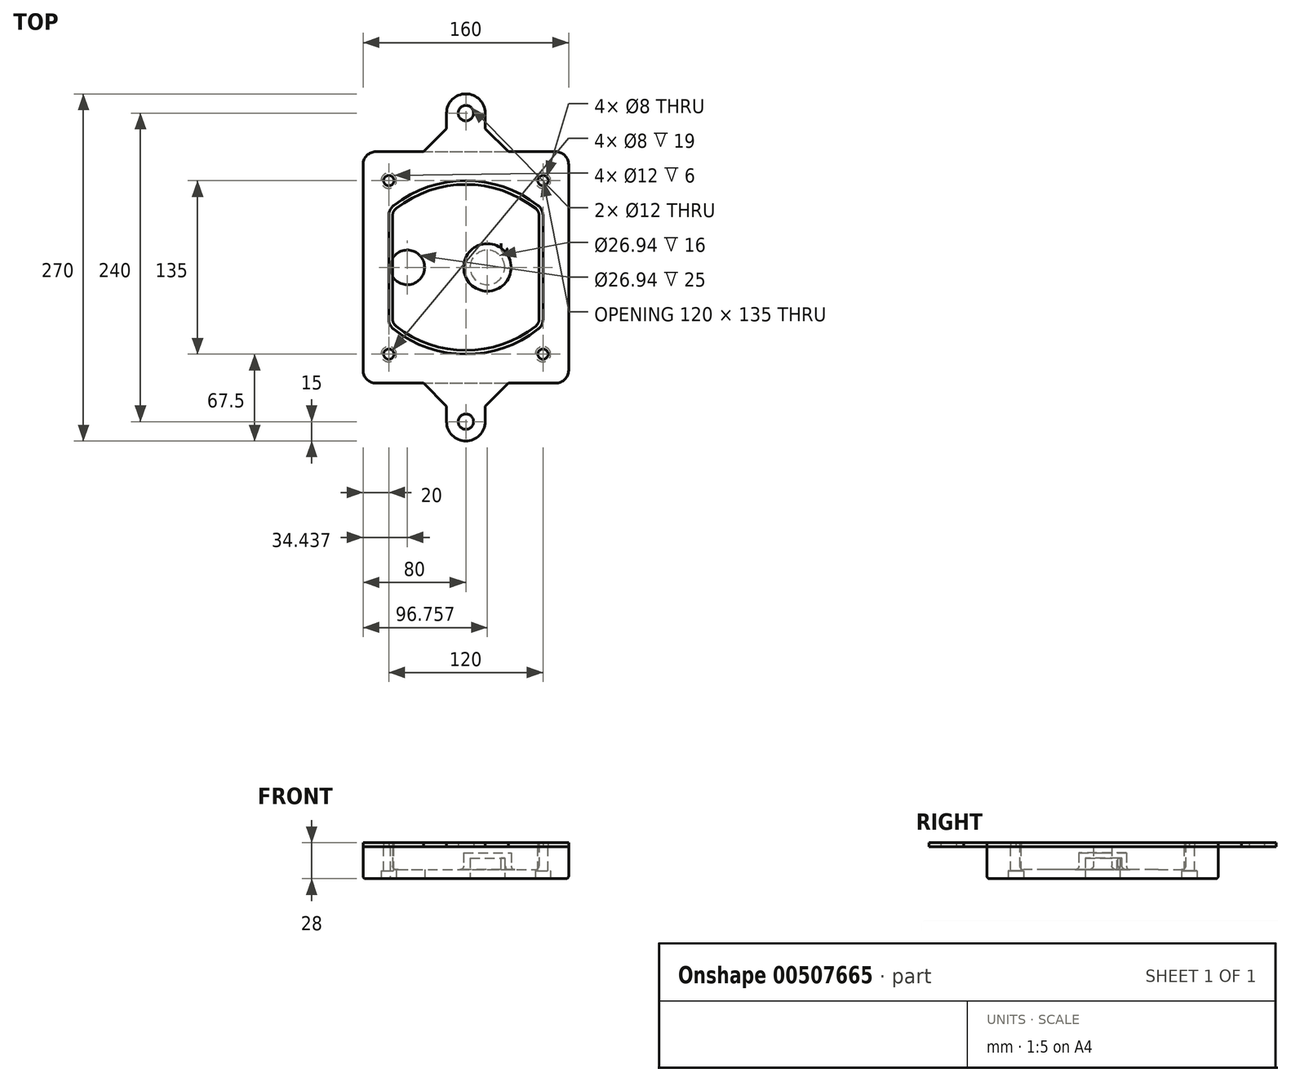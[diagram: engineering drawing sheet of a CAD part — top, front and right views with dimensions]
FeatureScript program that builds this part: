
annotation { "Feature Type Name" : "Feature", "Feature Type Description" : "" }
export const myFeature = defineFeature(function(context is Context, id is Id, definition is map)
    precondition{}
    {
        {
            var Q0;
            Q0=qCreatedBy(makeId("Top.planeOp"),FACE);
            var sketch = newSketch(context, id + "F0", { "sketchPlane" : qUnion([Q0])});
            skPoint(sketch, "E0.rect.middle", {"position": v(0, 0) * mm});
            skLineSegment(sketch, "E1.bottom", {"start": v(-70, -90) * mm, "end": v(70, -90) * mm});
            skLineSegment(sketch, "E1.top", {"start": v(-70, 90) * mm, "end": v(70, 90) * mm});
            skLineSegment(sketch, "E1.left", {"start": v(-80, -80) * mm, "end": v(-80, 80) * mm});
            skLineSegment(sketch, "E1.right", {"start": v(80, -80) * mm, "end": v(80, 80) * mm});
            skLineSegment(sketch, "E2", {"start": v(-80, 90) * mm, "end": v(80, -90) * mm, "construction": true});
            skLineSegment(sketch, "E3", {"start": v(80, 90) * mm, "end": v(-80, -90) * mm, "construction": true});
            skCircle(sketch, "E4", {"center": v(-60, 67.5) * mm, "radius": 4 * mm});
            skCircle(sketch, "E5", {"center": v(60, 67.5) * mm, "radius": 4 * mm});
            skCircle(sketch, "E6", {"center": v(60, -67.5) * mm, "radius": 4 * mm});
            skCircle(sketch, "E7", {"center": v(-60, -67.5) * mm, "radius": 4 * mm});
            skLineSegment(sketch, "E8", {"start": v(-60, 67.5) * mm, "end": v(60, 67.5) * mm, "construction": true});
            skLineSegment(sketch, "E9", {"start": v(60, 67.5) * mm, "end": v(60, -67.5) * mm, "construction": true});
            skLineSegment(sketch, "E10", {"start": v(60, -67.5) * mm, "end": v(-60, -67.5) * mm, "construction": true});
            skLineSegment(sketch, "E11", {"start": v(-60, -67.5) * mm, "end": v(-60, 67.5) * mm, "construction": true});
            skLineSegment(sketch, "E12", {"start": v(-60, 40.3) * mm, "end": v(-60, -40.3) * mm});
            skLineSegment(sketch, "E13", {"start": v(60, 40.3) * mm, "end": v(60, -40.3) * mm});
            skArc(sketch, "E14", {"start": v(56.15, 48.18) * mm, "mid": v(0, 67.5) * mm, "end": v(-56.15, 48.18) * mm});
            skArc(sketch, "E15", {"start": v(-56.15, -48.18) * mm, "mid": v(0, -67.5) * mm, "end": v(56.15, -48.18) * mm});
            skLineSegment(sketch, "E16", {"start": v(-60, 0) * mm, "end": v(60, 0) * mm, "construction": true});
            skPoint(sketch, "E17.visualSharp", {"position": v(-60, -45) * mm});
            skArc(sketch, "E17.filletArc", {"start": v(-60, -40.3) * mm, "mid": v(-58.99, -44.68) * mm, "end": v(-56.15, -48.18) * mm});
            skPoint(sketch, "E18.visualSharp", {"position": v(-60, 45) * mm});
            skArc(sketch, "E18.filletArc", {"start": v(-56.15, 48.18) * mm, "mid": v(-58.99, 44.68) * mm, "end": v(-60, 40.3) * mm});
            skPoint(sketch, "E19.visualSharp", {"position": v(60, 45) * mm});
            skArc(sketch, "E19.filletArc", {"start": v(60, 40.3) * mm, "mid": v(58.99, 44.68) * mm, "end": v(56.15, 48.18) * mm});
            skPoint(sketch, "E20.visualSharp", {"position": v(60, -45) * mm});
            skArc(sketch, "E20.filletArc", {"start": v(56.15, -48.18) * mm, "mid": v(58.99, -44.68) * mm, "end": v(60, -40.3) * mm});
            skPoint(sketch, "E21.visualSharp", {"position": v(-80, 90) * mm});
            skArc(sketch, "E21.filletArc", {"start": v(-70, 90) * mm, "mid": v(-77.07, 87.07) * mm, "end": v(-80, 80) * mm});
            skPoint(sketch, "E22.visualSharp", {"position": v(80, 90) * mm});
            skArc(sketch, "E22.filletArc", {"start": v(80, 80) * mm, "mid": v(77.07, 87.07) * mm, "end": v(70, 90) * mm});
            skPoint(sketch, "E23.visualSharp", {"position": v(80, -90) * mm});
            skArc(sketch, "E23.filletArc", {"start": v(70, -90) * mm, "mid": v(77.07, -87.07) * mm, "end": v(80, -80) * mm});
            skPoint(sketch, "E24.visualSharp", {"position": v(-80, -90) * mm});
            skArc(sketch, "E24.filletArc", {"start": v(-80, -80) * mm, "mid": v(-77.07, -87.07) * mm, "end": v(-70, -90) * mm});
            skArc(sketch, "E25.0", {"start": v(57, 40.3) * mm, "mid": v(56.3, 43.36) * mm, "end": v(54.3, 45.81) * mm});
            skLineSegment(sketch, "E25.1", {"start": v(57, 40.3) * mm, "end": v(57, -40.3) * mm});
            skArc(sketch, "E25.2", {"start": v(54.3, -45.81) * mm, "mid": v(56.3, -43.36) * mm, "end": v(57, -40.3) * mm});
            skArc(sketch, "E25.3", {"start": v(-54.3, -45.81) * mm, "mid": v(0, -64.5) * mm, "end": v(54.3, -45.81) * mm});
            skArc(sketch, "E25.4", {"start": v(-57, -40.3) * mm, "mid": v(-56.3, -43.36) * mm, "end": v(-54.3, -45.81) * mm});
            skArc(sketch, "E25.5", {"start": v(54.3, 45.81) * mm, "mid": v(0, 64.5) * mm, "end": v(-54.3, 45.81) * mm});
            skLineSegment(sketch, "E25.6", {"start": v(-57, 40.3) * mm, "end": v(-57, -40.3) * mm});
            skArc(sketch, "E25.7", {"start": v(-54.3, 45.81) * mm, "mid": v(-56.3, 43.36) * mm, "end": v(-57, 40.3) * mm});
            skArc(sketch, "E26.0", {"start": v(-58.62, 51.33) * mm, "mid": v(-62.58, 46.43) * mm, "end": v(-64, 40.3) * mm});
            skArc(sketch, "E26.1", {"start": v(58.62, 51.33) * mm, "mid": v(0, 71.5) * mm, "end": v(-58.62, 51.33) * mm});
            skArc(sketch, "E26.2", {"start": v(64, 40.3) * mm, "mid": v(62.58, 46.43) * mm, "end": v(58.62, 51.33) * mm});
            skLineSegment(sketch, "E26.3", {"start": v(64, 40.3) * mm, "end": v(64, -40.3) * mm});
            skArc(sketch, "E26.4", {"start": v(58.62, -51.33) * mm, "mid": v(62.58, -46.43) * mm, "end": v(64, -40.3) * mm});
            skLineSegment(sketch, "E26.5", {"start": v(-64, 40.3) * mm, "end": v(-64, -40.3) * mm});
            skArc(sketch, "E26.6", {"start": v(-58.62, -51.33) * mm, "mid": v(0, -71.5) * mm, "end": v(58.62, -51.33) * mm});
            skArc(sketch, "E26.7", {"start": v(-64, -40.3) * mm, "mid": v(-62.58, -46.43) * mm, "end": v(-58.62, -51.33) * mm});
            skSolve(sketch);
        }
        {
            var Q0;
            Q0=makeQuery(id+"F0.imprint","IMPRINT",FACE,{"disambiguationData":[TD([[makeQuery(id+"F0.imprint","IMPRINT",EDGE,{"derivedFrom":sQuery(id+"F0.wireOp",EDGE,"E1.bottom")}),1.0]])]});
            var Q1;
            Q1=makeQuery(id+"F0.imprint","IMPRINT",FACE,{"disambiguationData":[TD([[makeQuery(id+"F0.imprint","IMPRINT",EDGE,{"derivedFrom":sQuery(id+"F0.wireOp",EDGE,"E12")}),1.0]])]});
            var Q2;
            Q2=makeQuery(id+"F0.imprint","IMPRINT",FACE,{"disambiguationData":[TD([[makeQuery(id+"F0.imprint","IMPRINT",EDGE,{"derivedFrom":sQuery(id+"F0.wireOp",EDGE,"E25.0")}),1.0]])]});
            var Q3;
            Q3=makeQuery(id+"F0.imprint","IMPRINT",FACE,{"disambiguationData":[TD([[makeQuery(id+"F0.imprint","IMPRINT",EDGE,{"derivedFrom":sQuery(id+"F0.wireOp",EDGE,"E12")}),-1.0]])]});
            extrude(context, id + "F1", {"entities" : qUnion([Q0, Q1, Q2, Q3]), "oppositeDirection" : true, "depth" : 25 * mm});
        }
        {
            var Q0;
            Q0=makeQuery(id+"F0.imprint","IMPRINT",FACE,{"disambiguationData":[TD([[makeQuery(id+"F0.imprint","IMPRINT",EDGE,{"derivedFrom":sQuery(id+"F0.wireOp",EDGE,"E12")}),1.0]])]});
            extrude(context, id + "F2", {"entities" : qUnion([Q0]), "operationType" : NewBodyOperationType.ADD, "depth" : 3 * mm});
        }
        {
            var Q0;
            Q0=makeQuery(id+"F0.imprint","IMPRINT",FACE,{"disambiguationData":[TD([[makeQuery(id+"F0.imprint","IMPRINT",EDGE,{"derivedFrom":sQuery(id+"F0.wireOp",EDGE,"E25.0")}),1.0]])]});
            extrude(context, id + "F3", {"entities" : qUnion([Q0]), "operationType" : NewBodyOperationType.REMOVE, "oppositeDirection" : true, "depth" : 18 * mm});
        }
        {
            var Q0;
            Q0=makeQuery(id+"F2.opExtrude","CAP_FACE",FACE,{"disambiguationData":[OSD([sQuery(id+"F0.wireOp",EDGE,"E12"),sQuery(id+"F0.wireOp",EDGE,"E13"),sQuery(id+"F0.wireOp",EDGE,"E14"),sQuery(id+"F0.wireOp",EDGE,"E15"),sQuery(id+"F0.wireOp",EDGE,"E17.filletArc"),sQuery(id+"F0.wireOp",EDGE,"E18.filletArc"),sQuery(id+"F0.wireOp",EDGE,"E19.filletArc"),sQuery(id+"F0.wireOp",EDGE,"E20.filletArc"),sQuery(id+"F0.wireOp",EDGE,"E25.0"),sQuery(id+"F0.wireOp",EDGE,"E25.1"),sQuery(id+"F0.wireOp",EDGE,"E25.2"),sQuery(id+"F0.wireOp",EDGE,"E25.3"),sQuery(id+"F0.wireOp",EDGE,"E25.4"),sQuery(id+"F0.wireOp",EDGE,"E25.5"),sQuery(id+"F0.wireOp",EDGE,"E25.6"),sQuery(id+"F0.wireOp",EDGE,"E25.7")])],"isStart":false});
            var sketch = newSketch(context, id + "F4", { "sketchPlane" : qUnion([Q0])});
            skArc(sketch, "E27.0", {"start": v(-19.08, -46.97) * mm, "mid": v(0, -49.5) * mm, "end": v(19.08, -46.97) * mm});
            skArc(sketch, "E28.0", {"start": v(19.08, 46.97) * mm, "mid": v(0, 49.5) * mm, "end": v(-19.08, 46.97) * mm});
            skLineSegment(sketch, "E29", {"start": v(-25, 39.25) * mm, "end": v(-25, -39.25) * mm});
            skLineSegment(sketch, "E30", {"start": v(25, 39.25) * mm, "end": v(25, -39.25) * mm});
            skLineSegment(sketch, "E31", {"start": v(-25, 45.1) * mm, "end": v(25, 45.1) * mm, "construction": true});
            skLineSegment(sketch, "E32", {"start": v(-25, -45.1) * mm, "end": v(25, -45.1) * mm, "construction": true});
            skPoint(sketch, "E33.visualSharp", {"position": v(-25, 45.1) * mm});
            skArc(sketch, "E33.filletArc", {"start": v(-19.08, 46.97) * mm, "mid": v(-23.35, 44.11) * mm, "end": v(-25, 39.25) * mm});
            skPoint(sketch, "E34.visualSharp", {"position": v(25, 45.1) * mm});
            skArc(sketch, "E34.filletArc", {"start": v(25, 39.25) * mm, "mid": v(23.35, 44.11) * mm, "end": v(19.08, 46.97) * mm});
            skPoint(sketch, "E35.visualSharp", {"position": v(25, -45.1) * mm});
            skArc(sketch, "E35.filletArc", {"start": v(19.08, -46.97) * mm, "mid": v(23.35, -44.11) * mm, "end": v(25, -39.25) * mm});
            skPoint(sketch, "E36.visualSharp", {"position": v(-25, -45.1) * mm});
            skArc(sketch, "E36.filletArc", {"start": v(-25, -39.25) * mm, "mid": v(-23.35, -44.11) * mm, "end": v(-19.08, -46.97) * mm});
            skArc(sketch, "E37.0", {"start": v(54.3, 45.81) * mm, "mid": v(0, 64.5) * mm, "end": v(-54.3, 45.81) * mm});
            skArc(sketch, "E37.1", {"start": v(-54.3, 45.81) * mm, "mid": v(-56.3, 43.36) * mm, "end": v(-57, 40.3) * mm});
            skLineSegment(sketch, "E37.2", {"start": v(-57, 40.3) * mm, "end": v(-57, -40.3) * mm});
            skArc(sketch, "E37.3", {"start": v(-57, -40.3) * mm, "mid": v(-56.3, -43.36) * mm, "end": v(-54.3, -45.81) * mm});
            skArc(sketch, "E37.4", {"start": v(-54.3, -45.81) * mm, "mid": v(0, -64.5) * mm, "end": v(54.3, -45.81) * mm});
            skArc(sketch, "E37.5", {"start": v(54.3, -45.81) * mm, "mid": v(56.3, -43.36) * mm, "end": v(57, -40.3) * mm});
            skLineSegment(sketch, "E37.6", {"start": v(57, 40.3) * mm, "end": v(57, -40.3) * mm});
            skArc(sketch, "E37.7", {"start": v(57, 40.3) * mm, "mid": v(56.3, 43.36) * mm, "end": v(54.3, 45.81) * mm});
            skLineSegment(sketch, "E38.0", {"start": v(23, 39.25) * mm, "end": v(23, -39.25) * mm});
            skArc(sketch, "E38.1", {"start": v(18.56, -45.04) * mm, "mid": v(21.76, -42.9) * mm, "end": v(23, -39.25) * mm});
            skArc(sketch, "E38.2", {"start": v(-18.56, -45.04) * mm, "mid": v(0, -47.5) * mm, "end": v(18.56, -45.04) * mm});
            skArc(sketch, "E38.3", {"start": v(-23, -39.25) * mm, "mid": v(-21.76, -42.9) * mm, "end": v(-18.56, -45.04) * mm});
            skLineSegment(sketch, "E38.4", {"start": v(-23, 39.25) * mm, "end": v(-23, -39.25) * mm});
            skArc(sketch, "E38.5", {"start": v(23, 39.25) * mm, "mid": v(21.76, 42.9) * mm, "end": v(18.56, 45.04) * mm});
            skArc(sketch, "E38.6", {"start": v(-18.56, 45.04) * mm, "mid": v(-21.76, 42.9) * mm, "end": v(-23, 39.25) * mm});
            skArc(sketch, "E38.7", {"start": v(18.56, 45.04) * mm, "mid": v(0, 47.5) * mm, "end": v(-18.56, 45.04) * mm});
            skArc(sketch, "E39.0", {"start": v(21, 39.25) * mm, "mid": v(20.18, 41.68) * mm, "end": v(18.04, 43.1) * mm});
            skLineSegment(sketch, "E39.1", {"start": v(21, 39.25) * mm, "end": v(21, -39.25) * mm});
            skArc(sketch, "E39.2", {"start": v(18.04, -43.1) * mm, "mid": v(20.18, -41.68) * mm, "end": v(21, -39.25) * mm});
            skArc(sketch, "E39.3", {"start": v(-18.04, -43.1) * mm, "mid": v(0, -45.5) * mm, "end": v(18.04, -43.1) * mm});
            skArc(sketch, "E39.4", {"start": v(-21, -39.25) * mm, "mid": v(-20.18, -41.68) * mm, "end": v(-18.04, -43.1) * mm});
            skArc(sketch, "E39.5", {"start": v(18.04, 43.1) * mm, "mid": v(0, 45.5) * mm, "end": v(-18.04, 43.1) * mm});
            skLineSegment(sketch, "E39.6", {"start": v(-21, 39.25) * mm, "end": v(-21, -39.25) * mm});
            skArc(sketch, "E39.7", {"start": v(-18.04, 43.1) * mm, "mid": v(-20.18, 41.68) * mm, "end": v(-21, 39.25) * mm});
            skLineSegment(sketch, "E40", {"start": v(-25, 0) * mm, "end": v(25, 0) * mm, "construction": true});
            skLineSegment(sketch, "E41", {"start": v(-11, 5.5) * mm, "end": v(-11, 27.5) * mm});
            skLineSegment(sketch, "E42", {"start": v(-8, 30.5) * mm, "end": v(8, 30.5) * mm});
            skLineSegment(sketch, "E43", {"start": v(11, 27.5) * mm, "end": v(11, 13.5) * mm});
            skLineSegment(sketch, "E44", {"start": v(14, 10.5) * mm, "end": v(14, 10.5) * mm});
            skLineSegment(sketch, "E45", {"start": v(17, 7.5) * mm, "end": v(17, 5.5) * mm});
            skLineSegment(sketch, "E46", {"start": v(14, 2.5) * mm, "end": v(-8, 2.5) * mm});
            skPoint(sketch, "E47.visualSharp", {"position": v(-11, 30.5) * mm});
            skArc(sketch, "E47.filletArc", {"start": v(-8, 30.5) * mm, "mid": v(-10.12, 29.62) * mm, "end": v(-11, 27.5) * mm});
            skPoint(sketch, "E48.visualSharp", {"position": v(11, 30.5) * mm});
            skArc(sketch, "E48.filletArc", {"start": v(11, 27.5) * mm, "mid": v(10.12, 29.62) * mm, "end": v(8, 30.5) * mm});
            skPoint(sketch, "E49.visualSharp", {"position": v(11, 10.5) * mm});
            skArc(sketch, "E49.filletArc", {"start": v(11, 13.5) * mm, "mid": v(11.88, 11.38) * mm, "end": v(14, 10.5) * mm});
            skPoint(sketch, "E50.visualSharp", {"position": v(17, 10.5) * mm});
            skArc(sketch, "E50.filletArc", {"start": v(17, 7.5) * mm, "mid": v(16.12, 9.62) * mm, "end": v(14, 10.5) * mm});
            skPoint(sketch, "E51.visualSharp", {"position": v(17, 2.5) * mm});
            skArc(sketch, "E51.filletArc", {"start": v(14, 2.5) * mm, "mid": v(16.12, 3.38) * mm, "end": v(17, 5.5) * mm});
            skPoint(sketch, "E52.visualSharp", {"position": v(-11, 2.5) * mm});
            skArc(sketch, "E52.filletArc", {"start": v(-11, 5.5) * mm, "mid": v(-10.12, 3.38) * mm, "end": v(-8, 2.5) * mm});
            skLineSegment(sketch, "E53.0.MirrorCS", {"start": v(14, -2.5) * mm, "end": v(-8, -2.5) * mm});
            skArc(sketch, "E54.0.MirrorCS", {"start": v(-11, -5.5) * mm, "mid": v(-10.12, -3.38) * mm, "end": v(-8, -2.5) * mm});
            skLineSegment(sketch, "E55.0.MirrorCS", {"start": v(-11, -5.5) * mm, "end": v(-11, -27.5) * mm});
            skArc(sketch, "E56.0.MirrorCS", {"start": v(-8, -30.5) * mm, "mid": v(-10.12, -29.62) * mm, "end": v(-11, -27.5) * mm});
            skLineSegment(sketch, "E57.0.MirrorCS", {"start": v(-8, -30.5) * mm, "end": v(8, -30.5) * mm});
            skArc(sketch, "E58.0.MirrorCS", {"start": v(11, -27.5) * mm, "mid": v(10.12, -29.62) * mm, "end": v(8, -30.5) * mm});
            skLineSegment(sketch, "E59.0.MirrorCS", {"start": v(11, -27.5) * mm, "end": v(11, -13.5) * mm});
            skArc(sketch, "E60.0.MirrorCS", {"start": v(11, -13.5) * mm, "mid": v(11.88, -11.38) * mm, "end": v(14, -10.5) * mm});
            skArc(sketch, "E61.0.MirrorCS", {"start": v(17, -7.5) * mm, "mid": v(16.12, -9.62) * mm, "end": v(14, -10.5) * mm});
            skLineSegment(sketch, "E62.0.MirrorCS", {"start": v(17, -7.5) * mm, "end": v(17, -5.5) * mm});
            skArc(sketch, "E63.0.MirrorCS", {"start": v(14, -2.5) * mm, "mid": v(16.12, -3.38) * mm, "end": v(17, -5.5) * mm});
            skSolve(sketch);
        }
        {
            var Q0;
            Q0=makeQuery(id+"F4.imprint","IMPRINT",FACE,{"disambiguationData":[TD([[makeQuery(id+"F4.imprint","IMPRINT",EDGE,{"derivedFrom":sQuery(id+"F4.wireOp",EDGE,"E38.0")}),-1.0]])]});
            extrude(context, id + "F5", {"entities" : qUnion([Q0]), "operationType" : NewBodyOperationType.REMOVE, "oppositeDirection" : true, "depth" : 2 * mm});
        }
        {
            var Q0;
            Q0=makeQuery(id+"F1.opExtrude","CAP_FACE",FACE,{"disambiguationData":[OSD([sQuery(id+"F0.wireOp",EDGE,"E1.bottom"),sQuery(id+"F0.wireOp",EDGE,"E1.top"),sQuery(id+"F0.wireOp",EDGE,"E1.left"),sQuery(id+"F0.wireOp",EDGE,"E1.right"),sQuery(id+"F0.wireOp",EDGE,"E4"),sQuery(id+"F0.wireOp",EDGE,"E5"),sQuery(id+"F0.wireOp",EDGE,"E6"),sQuery(id+"F0.wireOp",EDGE,"E7"),sQuery(id+"F0.wireOp",EDGE,"E21.filletArc"),sQuery(id+"F0.wireOp",EDGE,"E22.filletArc"),sQuery(id+"F0.wireOp",EDGE,"E23.filletArc"),sQuery(id+"F0.wireOp",EDGE,"E24.filletArc")])],"isStart":false});
            var sketch = newSketch(context, id + "F6", { "sketchPlane" : qUnion([Q0])});
            skCircle(sketch, "E64", {"center": v(16.76, 0) * mm, "radius": 13.47 * mm});
            skCircle(sketch, "E65", {"center": v(-45.56, 0) * mm, "radius": 13.47 * mm});
            skLineSegment(sketch, "E66", {"start": v(80, 0) * mm, "end": v(-80, 0) * mm});
            skCircle(sketch, "E67", {"center": v(16.76, 0) * mm, "radius": 18.47 * mm});
            skCircle(sketch, "E68", {"center": v(60, -67.5) * mm, "radius": 6 * mm});
            skCircle(sketch, "E69", {"center": v(-60, -67.5) * mm, "radius": 6 * mm});
            skCircle(sketch, "E70", {"center": v(-60, 67.5) * mm, "radius": 6 * mm});
            skCircle(sketch, "E71", {"center": v(60, 67.5) * mm, "radius": 6 * mm});
            skSolve(sketch);
        }
        {
            var Q0;
            {var subQ1=sQuery(id+"F6.wireOp",EDGE,"E66");var subQ4=sQuery(id+"F6.wireOp",EDGE,"E64");var subQ6=makeQuery(id+"F6.imprint","INTERSECT",VERTEX,{"disambiguationData":[OD(0.0)],"derivedFrom":[subQ4,subQ1]});Q0=makeQuery(id+"F6.imprint","IMPRINT",FACE,{"disambiguationData":[TD([[makeQuery(id+"F6.imprint","IMPRINT",EDGE,{"disambiguationData":[TD([[subQ6,-1.0]])],"derivedFrom":subQ4}),-1.0]])]});}
            var Q1;
            {var subQ0=sQuery(id+"F6.wireOp",EDGE,"E66");var subQ1=sQuery(id+"F6.wireOp",EDGE,"E64");var subQ3=makeQuery(id+"F6.imprint","INTERSECT",VERTEX,{"disambiguationData":[OD(0.0)],"derivedFrom":[subQ1,subQ0]});Q1=makeQuery(id+"F6.imprint","IMPRINT",FACE,{"disambiguationData":[TD([[makeQuery(id+"F6.imprint","IMPRINT",EDGE,{"disambiguationData":[TD([[subQ3,-1.0]])],"derivedFrom":subQ1}),1.0]])]});}
            var Q2;
            {var subQ0=sQuery(id+"F6.wireOp",EDGE,"E66");var subQ1=sQuery(id+"F6.wireOp",EDGE,"E64");var subQ3=makeQuery(id+"F6.imprint","INTERSECT",VERTEX,{"disambiguationData":[OD(0.0)],"derivedFrom":[subQ1,subQ0]});Q2=makeQuery(id+"F6.imprint","IMPRINT",FACE,{"disambiguationData":[TD([[makeQuery(id+"F6.imprint","IMPRINT",EDGE,{"disambiguationData":[TD([[subQ3,1.0]])],"derivedFrom":subQ1}),1.0]])]});}
            var Q3;
            {var subQ1=sQuery(id+"F6.wireOp",EDGE,"E66");var subQ4=sQuery(id+"F6.wireOp",EDGE,"E64");var subQ6=makeQuery(id+"F6.imprint","INTERSECT",VERTEX,{"disambiguationData":[OD(0.0)],"derivedFrom":[subQ4,subQ1]});Q3=makeQuery(id+"F6.imprint","IMPRINT",FACE,{"disambiguationData":[TD([[makeQuery(id+"F6.imprint","IMPRINT",EDGE,{"disambiguationData":[TD([[subQ6,1.0]])],"derivedFrom":subQ4}),-1.0]])]});}
            extrude(context, id + "F7", {"entities" : qUnion([Q0, Q1, Q2, Q3]), "operationType" : NewBodyOperationType.ADD, "oppositeDirection" : true, "depth" : 20 * mm});
        }
        {
            var Q0;
            {var subQ0=sQuery(id+"F6.wireOp",EDGE,"E66");var subQ1=sQuery(id+"F6.wireOp",EDGE,"E64");var subQ3=makeQuery(id+"F6.imprint","INTERSECT",VERTEX,{"disambiguationData":[OD(0.0)],"derivedFrom":[subQ1,subQ0]});Q0=makeQuery(id+"F6.imprint","IMPRINT",FACE,{"disambiguationData":[TD([[makeQuery(id+"F6.imprint","IMPRINT",EDGE,{"disambiguationData":[TD([[subQ3,-1.0]])],"derivedFrom":subQ1}),1.0]])]});}
            var Q1;
            {var subQ0=sQuery(id+"F6.wireOp",EDGE,"E66");var subQ1=sQuery(id+"F6.wireOp",EDGE,"E64");var subQ3=makeQuery(id+"F6.imprint","INTERSECT",VERTEX,{"disambiguationData":[OD(0.0)],"derivedFrom":[subQ1,subQ0]});Q1=makeQuery(id+"F6.imprint","IMPRINT",FACE,{"disambiguationData":[TD([[makeQuery(id+"F6.imprint","IMPRINT",EDGE,{"disambiguationData":[TD([[subQ3,1.0]])],"derivedFrom":subQ1}),1.0]])]});}
            extrude(context, id + "F8", {"entities" : qUnion([Q0, Q1]), "operationType" : NewBodyOperationType.REMOVE, "oppositeDirection" : true, "depth" : 16 * mm});
        }
        {
            var Q0;
            {var subQ0=sQuery(id+"F6.wireOp",EDGE,"E66");var subQ1=sQuery(id+"F6.wireOp",EDGE,"E65");var subQ3=makeQuery(id+"F6.imprint","INTERSECT",VERTEX,{"disambiguationData":[OD(0.0)],"derivedFrom":[subQ1,subQ0]});Q0=makeQuery(id+"F6.imprint","IMPRINT",FACE,{"disambiguationData":[TD([[makeQuery(id+"F6.imprint","IMPRINT",EDGE,{"disambiguationData":[TD([[subQ3,-1.0]])],"derivedFrom":subQ1}),1.0]])]});}
            var Q1;
            {var subQ0=sQuery(id+"F6.wireOp",EDGE,"E66");var subQ1=sQuery(id+"F6.wireOp",EDGE,"E65");var subQ3=makeQuery(id+"F6.imprint","INTERSECT",VERTEX,{"disambiguationData":[OD(0.0)],"derivedFrom":[subQ1,subQ0]});Q1=makeQuery(id+"F6.imprint","IMPRINT",FACE,{"disambiguationData":[TD([[makeQuery(id+"F6.imprint","IMPRINT",EDGE,{"disambiguationData":[TD([[subQ3,1.0]])],"derivedFrom":subQ1}),1.0]])]});}
            extrude(context, id + "F9", {"entities" : qUnion([Q0, Q1]), "operationType" : NewBodyOperationType.REMOVE, "oppositeDirection" : true, "depth" : 25 * mm});
        }
        {
            var Q0;
            Q0=makeQuery(id+"F6.imprint","IMPRINT",FACE,{"disambiguationData":[TD([[makeQuery(id+"F6.imprint","IMPRINT",EDGE,{"derivedFrom":sQuery(id+"F6.wireOp",EDGE,"E68")}),1.0]])]});
            var Q1;
            Q1=makeQuery(id+"F6.imprint","IMPRINT",FACE,{"disambiguationData":[TD([[makeQuery(id+"F6.imprint","IMPRINT",EDGE,{"derivedFrom":makeQuery(id+"F1.opExtrude","CAP_EDGE",EDGE,{"disambiguationData":[OSD([sQuery(id+"F0.wireOp",EDGE,"E5")])],"isStart":false})}),-1.0]])]});
            var Q2;
            Q2=makeQuery(id+"F6.imprint","IMPRINT",FACE,{"disambiguationData":[TD([[makeQuery(id+"F6.imprint","IMPRINT",EDGE,{"derivedFrom":sQuery(id+"F6.wireOp",EDGE,"E69")}),1.0]])]});
            var Q3;
            Q3=makeQuery(id+"F6.imprint","IMPRINT",FACE,{"disambiguationData":[TD([[makeQuery(id+"F6.imprint","IMPRINT",EDGE,{"derivedFrom":makeQuery(id+"F1.opExtrude","CAP_EDGE",EDGE,{"disambiguationData":[OSD([sQuery(id+"F0.wireOp",EDGE,"E4")])],"isStart":false})}),-1.0]])]});
            var Q4;
            Q4=makeQuery(id+"F6.imprint","IMPRINT",FACE,{"disambiguationData":[TD([[makeQuery(id+"F6.imprint","IMPRINT",EDGE,{"derivedFrom":sQuery(id+"F6.wireOp",EDGE,"E70")}),1.0]])]});
            var Q5;
            Q5=makeQuery(id+"F6.imprint","IMPRINT",FACE,{"disambiguationData":[TD([[makeQuery(id+"F6.imprint","IMPRINT",EDGE,{"derivedFrom":makeQuery(id+"F1.opExtrude","CAP_EDGE",EDGE,{"disambiguationData":[OSD([sQuery(id+"F0.wireOp",EDGE,"E7")])],"isStart":false})}),-1.0]])]});
            var Q6;
            Q6=makeQuery(id+"F6.imprint","IMPRINT",FACE,{"disambiguationData":[TD([[makeQuery(id+"F6.imprint","IMPRINT",EDGE,{"derivedFrom":sQuery(id+"F6.wireOp",EDGE,"E71")}),1.0]])]});
            var Q7;
            Q7=makeQuery(id+"F6.imprint","IMPRINT",FACE,{"disambiguationData":[TD([[makeQuery(id+"F6.imprint","IMPRINT",EDGE,{"derivedFrom":makeQuery(id+"F1.opExtrude","CAP_EDGE",EDGE,{"disambiguationData":[OSD([sQuery(id+"F0.wireOp",EDGE,"E6")])],"isStart":false})}),-1.0]])]});
            extrude(context, id + "F10", {"entities" : qUnion([Q0, Q1, Q2, Q3, Q4, Q5, Q6, Q7]), "operationType" : NewBodyOperationType.REMOVE, "oppositeDirection" : true, "depth" : 6 * mm});
        }
        {
            var Q0;
            Q0=makeQuery(id+"F8.boolean.opBoolean","COPY",FACE,{"derivedFrom":makeQuery(id+"F8.opExtrude","CAP_FACE",FACE,{"disambiguationData":[OSD([sQuery(id+"F6.wireOp",EDGE,"E64")])],"isStart":false})});
            var sketch = newSketch(context, id + "F11", { "sketchPlane" : qUnion([Q0])});
            skArc(sketch, "E72.0", {"start": v(29.38, -13.48) * mm, "mid": v(4.86, 14.13) * mm, "end": v(27.9, -14.73) * mm});
            skArc(sketch, "E72.1", {"start": v(27.55, -14.98) * mm, "mid": v(6.04, 15.04) * mm, "end": v(27.4, -15.1) * mm});
            skLineSegment(sketch, "E73", {"start": v(27.55, -14.98) * mm, "end": v(37.34, -14.98) * mm});
            skLineSegment(sketch, "E74.0", {"start": v(37.7, -14.73) * mm, "end": v(27.9, -14.73) * mm});
            skArc(sketch, "E74.1", {"start": v(37.7, -14.73) * mm, "mid": v(39.81, -13.85) * mm, "end": v(40.7, -11.73) * mm});
            skLineSegment(sketch, "E74.2", {"start": v(40.7, -9.73) * mm, "end": v(40.7, -11.73) * mm});
            skArc(sketch, "E74.3", {"start": v(40.7, -9.73) * mm, "mid": v(39.81, -7.6) * mm, "end": v(37.7, -6.73) * mm});
            skArc(sketch, "E74.4", {"start": v(29.38, -14.43) * mm, "mid": v(37.38, -14.74) * mm, "end": v(37.7, -6.73) * mm});
            skLineSegment(sketch, "E74.5", {"start": v(29.38, -13.48) * mm, "end": v(29.38, -14.43) * mm});
            skLineSegment(sketch, "E74.7", {"start": v(37.34, -14.98) * mm, "end": v(27.55, -14.98) * mm});
            skArc(sketch, "E74.8", {"start": v(37.34, -14.98) * mm, "mid": v(30.95, -12.54) * mm, "end": v(33.4, -6.15) * mm});
            skLineSegment(sketch, "E74.9", {"start": v(33.4, -8.15) * mm, "end": v(33.4, -6.15) * mm});
            skArc(sketch, "E74.10", {"start": v(33.4, -8.15) * mm, "mid": v(32.52, -10.27) * mm, "end": v(30.4, -11.15) * mm});
            skArc(sketch, "E74.11", {"start": v(27.4, -14.15) * mm, "mid": v(28.28, -12.03) * mm, "end": v(30.4, -11.15) * mm});
            skLineSegment(sketch, "E74.12", {"start": v(27.4, -15.1) * mm, "end": v(27.4, -14.15) * mm});
            skPoint(sketch, "E75.orphan", {"position": v(27.4, -28.15) * mm});
            skPoint(sketch, "E76.orphan", {"position": v(15.34, -14.98) * mm});
            skPoint(sketch, "E77.orphan", {"position": v(15.7, -14.73) * mm});
            skPoint(sketch, "E78.orphan", {"position": v(29.38, -0.43) * mm});
            skSolve(sketch);
        }
        {
            var Q0;
            {var subQ7=sQuery(id+"F11.wireOp",EDGE,"E72.0");var subQ14=sQuery(id+"F11.wireOp",EDGE,"E72.1");var subQ16=sQuery(id+"F11.wireOp",EDGE,"E74.1");var subQ18=sQuery(id+"F11.wireOp",EDGE,"E74.8");Q0=qUnion([makeQuery(id+"F11.imprint","IMPRINT",FACE,{"disambiguationData":[TD([[makeQuery(id+"F11.imprint","IMPRINT",EDGE,{"derivedFrom":subQ7}),1.0]])]}),makeQuery(id+"F11.imprint","IMPRINT",FACE,{"disambiguationData":[TD([[makeQuery(id+"F11.imprint","IMPRINT",EDGE,{"derivedFrom":subQ14}),1.0]])]}),makeQuery(id+"F11.imprint","IMPRINT",FACE,{"disambiguationData":[TD([[makeQuery(id+"F11.imprint","IMPRINT",EDGE,{"derivedFrom":subQ16}),1.0]])]}),makeQuery(id+"F11.imprint","IMPRINT",FACE,{"disambiguationData":[TD([[makeQuery(id+"F11.imprint","IMPRINT",EDGE,{"derivedFrom":subQ18}),-1.0]])]})]);}
            var Q1;
            Q1=makeQuery(id+"FRSeB4H3tOQNN8t_1.boolean.opBoolean","SPLIT",FACE,{"disambiguationData":[TD([makeQuery(id+"FRSeB4H3tOQNN8t_1.opExtrude","SWEPT_FACE",FACE,{"disambiguationData":[OSD([sQuery(id+"F4.wireOp",EDGE,"E41")])]})])],"derivedFrom":makeQuery(id+"F3.boolean.opBoolean","COPY",FACE,{"derivedFrom":makeQuery(id+"F3.opExtrude","CAP_FACE",FACE,{"disambiguationData":[OSD([sQuery(id+"F0.wireOp",EDGE,"E25.0"),sQuery(id+"F0.wireOp",EDGE,"E25.1"),sQuery(id+"F0.wireOp",EDGE,"E25.2"),sQuery(id+"F0.wireOp",EDGE,"E25.3"),sQuery(id+"F0.wireOp",EDGE,"E25.4"),sQuery(id+"F0.wireOp",EDGE,"E25.5"),sQuery(id+"F0.wireOp",EDGE,"E25.6"),sQuery(id+"F0.wireOp",EDGE,"E25.7")])],"isStart":false})})});
            extrude(context, id + "F12", {"entities" : qUnion([Q0]), "operationType" : NewBodyOperationType.REMOVE, "endBound" : BoundingType.UP_TO_SURFACE, "endBoundEntityFace" : qUnion([Q1]), "depth" : 25 * mm});
        }
        {
            var Q0;
            Q0=makeQuery(id+"F3.boolean.opBoolean","COPY",EDGE,{"derivedFrom":makeQuery(id+"F3.opExtrude","CAP_EDGE",EDGE,{"disambiguationData":[OSD([sQuery(id+"F0.wireOp",EDGE,"E25.6")])],"isStart":false})});
            var Q1;
            Q1=makeQuery(id+"F7.boolean.opBoolean","INTERSECT",EDGE,{"derivedFrom":[makeQuery(id+"FRSeB4H3tOQNN8t_1.opExtrude","SWEPT_FACE",FACE,{"disambiguationData":[OSD([sQuery(id+"F4.wireOp",EDGE,"E30")])]}),makeQuery(id+"F7.opExtrude","CAP_FACE",FACE,{"disambiguationData":[OSD([sQuery(id+"F6.wireOp",EDGE,"E67")])],"isStart":false})]});
            var Q2;
            Q2=makeQuery(id+"F7.boolean.opBoolean","INTERSECT",EDGE,{"disambiguationData":[OD(1.0)],"derivedFrom":[makeQuery(id+"FRSeB4H3tOQNN8t_1.opExtrude","SWEPT_FACE",FACE,{"disambiguationData":[OSD([sQuery(id+"F4.wireOp",EDGE,"E30")])]}),makeQuery(id+"F7.opExtrude","SWEPT_FACE",FACE,{"disambiguationData":[OSD([sQuery(id+"F6.wireOp",EDGE,"E67")])]})]});
            var Q3;
            {var subQ0=makeQuery(id+"F3.boolean.opBoolean","COPY",FACE,{"derivedFrom":makeQuery(id+"F3.opExtrude","CAP_FACE",FACE,{"disambiguationData":[OSD([sQuery(id+"F0.wireOp",EDGE,"E25.0"),sQuery(id+"F0.wireOp",EDGE,"E25.1"),sQuery(id+"F0.wireOp",EDGE,"E25.2"),sQuery(id+"F0.wireOp",EDGE,"E25.3"),sQuery(id+"F0.wireOp",EDGE,"E25.4"),sQuery(id+"F0.wireOp",EDGE,"E25.5"),sQuery(id+"F0.wireOp",EDGE,"E25.6"),sQuery(id+"F0.wireOp",EDGE,"E25.7")])],"isStart":false})});var subQ1=sQuery(id+"F4.wireOp",EDGE,"E30");Q3=makeQuery(id+"F7.boolean.opBoolean","SPLIT",EDGE,{"disambiguationData":[TD([makeQuery(id+"FRSeB4H3tOQNN8t_1.opExtrude","SWEPT_FACE",FACE,{"disambiguationData":[OSD([sQuery(id+"F4.wireOp",EDGE,"E35.filletArc")])]})])],"derivedFrom":makeQuery(id+"FRSeB4H3tOQNN8t_1.opExtrude","TWEAK_EDGE",EDGE,{"derivedFrom":[subQ0,makeQuery(id+"F4.imprint","IMPRINT",EDGE,{"derivedFrom":subQ1})]})});}
            var Q4;
            {var subQ0=sQuery(id+"F0.wireOp",EDGE,"E25.0");var subQ1=sQuery(id+"F0.wireOp",EDGE,"E25.1");var subQ2=sQuery(id+"F0.wireOp",EDGE,"E25.2");var subQ3=sQuery(id+"F0.wireOp",EDGE,"E25.3");var subQ4=sQuery(id+"F0.wireOp",EDGE,"E25.4");var subQ5=sQuery(id+"F0.wireOp",EDGE,"E25.5");var subQ6=sQuery(id+"F0.wireOp",EDGE,"E25.6");var subQ7=sQuery(id+"F0.wireOp",EDGE,"E25.7");Q4=makeQuery(id+"F7.boolean.opBoolean","INTERSECT",EDGE,{"derivedFrom":[makeQuery(id+"FRSeB4H3tOQNN8t_1.boolean.opBoolean","SPLIT",FACE,{"disambiguationData":[TD([makeQuery(id+"F2.opExtrude","SWEPT_FACE",FACE,{"disambiguationData":[OSD([subQ0])]})])],"derivedFrom":makeQuery(id+"F3.boolean.opBoolean","COPY",FACE,{"derivedFrom":makeQuery(id+"F3.opExtrude","CAP_FACE",FACE,{"disambiguationData":[OSD([subQ0,subQ1,subQ2,subQ3,subQ4,subQ5,subQ6,subQ7])],"isStart":false})})}),makeQuery(id+"F7.opExtrude","SWEPT_FACE",FACE,{"disambiguationData":[OSD([sQuery(id+"F6.wireOp",EDGE,"E67")])]})]});}
            var Q5;
            Q5=makeQuery(id+"F7.boolean.opBoolean","INTERSECT",EDGE,{"disambiguationData":[OD(0.0)],"derivedFrom":[makeQuery(id+"FRSeB4H3tOQNN8t_1.opExtrude","SWEPT_FACE",FACE,{"disambiguationData":[OSD([sQuery(id+"F4.wireOp",EDGE,"E30")])]}),makeQuery(id+"F7.opExtrude","SWEPT_FACE",FACE,{"disambiguationData":[OSD([sQuery(id+"F6.wireOp",EDGE,"E67")])]})]});
            fillet(context, id + "F13", {"entities" : qUnion([Q0, Q1, Q2, Q3, Q4, Q5]), "radius" : 3 * mm, "tangentPropagation" : true, "allowEdgeOverflow" : false});
        }
        {
            var Q0;
            Q0=makeQuery(id+"F1.opExtrude","CAP_EDGE",EDGE,{"disambiguationData":[OSD([sQuery(id+"F0.wireOp",EDGE,"E1.bottom")])],"isStart":false});
            fillet(context, id + "F14", {"entities" : qUnion([Q0]), "radius" : 2 * mm, "tangentPropagation" : true, "allowEdgeOverflow" : false});
        }
        {
            var Q0;
            {var subQ0=sQuery(id+"F0.wireOp",EDGE,"E21.filletArc");var subQ1=sQuery(id+"F0.wireOp",EDGE,"E7");var subQ2=sQuery(id+"F0.wireOp",EDGE,"E6");var subQ3=sQuery(id+"F0.wireOp",EDGE,"E5");var subQ4=sQuery(id+"F0.wireOp",EDGE,"E4");var subQ5=sQuery(id+"F0.wireOp",EDGE,"E22.filletArc");var subQ6=sQuery(id+"F0.wireOp",EDGE,"E1.bottom");var subQ7=sQuery(id+"F0.wireOp",EDGE,"E1.right");var subQ8=sQuery(id+"F0.wireOp",EDGE,"E1.top");var subQ9=sQuery(id+"F0.wireOp",EDGE,"E1.left");var subQ10=sQuery(id+"F0.wireOp",EDGE,"E23.filletArc");var subQ11=sQuery(id+"F0.wireOp",EDGE,"E24.filletArc");Q0=makeQuery(id+"F2.boolean.opBoolean","SPLIT",FACE,{"disambiguationData":[TD([makeQuery(id+"F1.opExtrude","SWEPT_FACE",FACE,{"disambiguationData":[OSD([subQ6])]})])],"derivedFrom":makeQuery(id+"F1.opExtrude","CAP_FACE",FACE,{"disambiguationData":[OSD([subQ6,subQ8,subQ9,subQ7,subQ4,subQ3,subQ2,subQ1,subQ0,subQ5,subQ10,subQ11])],"isStart":true})});}
            var sketch = newSketch(context, id + "F15", { "sketchPlane" : qUnion([Q0])});
            skLineSegment(sketch, "E79.0", {"start": v(-70, 90) * mm, "end": v(70, 90) * mm});
            skArc(sketch, "E79.1", {"start": v(-70, 90) * mm, "mid": v(-77.07, 87.07) * mm, "end": v(-80, 80) * mm});
            skLineSegment(sketch, "E79.2", {"start": v(-80, -80) * mm, "end": v(-80, 80) * mm});
            skArc(sketch, "E79.3", {"start": v(-80, -80) * mm, "mid": v(-77.07, -87.07) * mm, "end": v(-70, -90) * mm});
            skLineSegment(sketch, "E79.4", {"start": v(-70, -90) * mm, "end": v(70, -90) * mm});
            skArc(sketch, "E79.5", {"start": v(70, -90) * mm, "mid": v(77.07, -87.07) * mm, "end": v(80, -80) * mm});
            skLineSegment(sketch, "E79.6", {"start": v(80, -80) * mm, "end": v(80, 80) * mm});
            skArc(sketch, "E79.7", {"start": v(80, 80) * mm, "mid": v(77.07, 87.07) * mm, "end": v(70, 90) * mm});
            skCircle(sketch, "E79.8", {"center": v(60, 67.5) * mm, "radius": 4 * mm});
            skCircle(sketch, "E79.9", {"center": v(60, -67.5) * mm, "radius": 4 * mm});
            skCircle(sketch, "E79.10", {"center": v(-60, -67.5) * mm, "radius": 4 * mm});
            skCircle(sketch, "E79.11", {"center": v(-60, 67.5) * mm, "radius": 4 * mm});
            skArc(sketch, "E79.12", {"start": v(56.15, 48.18) * mm, "mid": v(0, 67.5) * mm, "end": v(-56.15, 48.18) * mm});
            skArc(sketch, "E79.13", {"start": v(-56.15, 48.18) * mm, "mid": v(-58.99, 44.68) * mm, "end": v(-60, 40.3) * mm});
            skLineSegment(sketch, "E79.14", {"start": v(-60, 40.3) * mm, "end": v(-60, -40.3) * mm});
            skArc(sketch, "E79.15", {"start": v(-60, -40.3) * mm, "mid": v(-58.99, -44.68) * mm, "end": v(-56.15, -48.18) * mm});
            skArc(sketch, "E79.16", {"start": v(-56.15, -48.18) * mm, "mid": v(0, -67.5) * mm, "end": v(56.15, -48.18) * mm});
            skArc(sketch, "E79.17", {"start": v(56.15, -48.18) * mm, "mid": v(58.99, -44.68) * mm, "end": v(60, -40.3) * mm});
            skLineSegment(sketch, "E79.18", {"start": v(60, 40.3) * mm, "end": v(60, -40.3) * mm});
            skArc(sketch, "E79.19", {"start": v(60, 40.3) * mm, "mid": v(58.99, 44.68) * mm, "end": v(56.15, 48.18) * mm});
            skLineSegment(sketch, "E80", {"start": v(0, 90) * mm, "end": v(0, 120) * mm, "construction": true});
            skPoint(sketch, "E80.endSnap0", {"position": v(0, 90) * mm});
            skLineSegment(sketch, "E81", {"start": v(-33, 90) * mm, "end": v(-15, 108) * mm});
            skLineSegment(sketch, "E82", {"start": v(-15, 108) * mm, "end": v(-15, 120) * mm});
            skLineSegment(sketch, "E83", {"start": v(33, 90) * mm, "end": v(15, 108) * mm});
            skLineSegment(sketch, "E84", {"start": v(15, 108) * mm, "end": v(15, 120) * mm});
            skArc(sketch, "E85", {"start": v(15, 120) * mm, "mid": v(0, 135) * mm, "end": v(-15, 120) * mm});
            skCircle(sketch, "E86", {"center": v(0, 120) * mm, "radius": 6 * mm});
            skLineSegment(sketch, "E87", {"start": v(-80, 0) * mm, "end": v(80, 0) * mm, "construction": true});
            skLineSegment(sketch, "E88.MirrorCS", {"start": v(-33, -90) * mm, "end": v(-15, -108) * mm});
            skLineSegment(sketch, "E89.MirrorCS", {"start": v(-15, -108) * mm, "end": v(-15, -120) * mm});
            skArc(sketch, "E90.MirrorCS", {"start": v(15, -120) * mm, "mid": v(0, -135) * mm, "end": v(-15, -120) * mm});
            skLineSegment(sketch, "E91.MirrorCS", {"start": v(15, -108) * mm, "end": v(15, -120) * mm});
            skLineSegment(sketch, "E92.MirrorCS", {"start": v(33, -90) * mm, "end": v(15, -108) * mm});
            skCircle(sketch, "E93.MirrorC", {"center": v(0, -120) * mm, "radius": 6 * mm});
            skLineSegment(sketch, "E94.MirrorCS", {"start": v(0, -90) * mm, "end": v(0, -120) * mm, "construction": true});
            skSolve(sketch);
        }
        {
            var Q0;
            {var subQ0=sQuery(id+"F15.wireOp",EDGE,"E81");Q0=makeQuery(id+"F15.imprint","IMPRINT",FACE,{"disambiguationData":[TD([[makeQuery(id+"F15.imprint","IMPRINT",EDGE,{"derivedFrom":subQ0}),-1.0]])]});}
            var Q1;
            Q1=makeQuery(id+"F15.imprint","IMPRINT",FACE,{"disambiguationData":[TD([[makeQuery(id+"F15.imprint","IMPRINT",EDGE,{"derivedFrom":sQuery(id+"F15.wireOp",EDGE,"E89.MirrorCS")}),1.0]])]});
            var Q2;
            {var subQ1=sQuery(id+"F15.wireOp",EDGE,"E79.1");Q2=makeQuery(id+"F15.imprint","IMPRINT",FACE,{"disambiguationData":[TD([[makeQuery(id+"F15.imprint","IMPRINT",EDGE,{"derivedFrom":subQ1}),1.0]])]});}
            var Q3;
            Q3=makeQuery(id+"F2.opExtrude","CAP_FACE",FACE,{"disambiguationData":[OSD([sQuery(id+"F0.wireOp",EDGE,"E12"),sQuery(id+"F0.wireOp",EDGE,"E13"),sQuery(id+"F0.wireOp",EDGE,"E14"),sQuery(id+"F0.wireOp",EDGE,"E15"),sQuery(id+"F0.wireOp",EDGE,"E17.filletArc"),sQuery(id+"F0.wireOp",EDGE,"E18.filletArc"),sQuery(id+"F0.wireOp",EDGE,"E19.filletArc"),sQuery(id+"F0.wireOp",EDGE,"E20.filletArc"),sQuery(id+"F0.wireOp",EDGE,"E25.0"),sQuery(id+"F0.wireOp",EDGE,"E25.1"),sQuery(id+"F0.wireOp",EDGE,"E25.2"),sQuery(id+"F0.wireOp",EDGE,"E25.3"),sQuery(id+"F0.wireOp",EDGE,"E25.4"),sQuery(id+"F0.wireOp",EDGE,"E25.5"),sQuery(id+"F0.wireOp",EDGE,"E25.6"),sQuery(id+"F0.wireOp",EDGE,"E25.7")])],"isStart":false});
            extrude(context, id + "F16", {"entities" : qUnion([Q0, Q1, Q2]), "endBound" : BoundingType.UP_TO_SURFACE, "endBoundEntityFace" : qUnion([Q3]), "depth" : 25 * mm, "offsetDistance" : 25 * mm});
        }
    });
